# Revit family: 0040331 Sylvania Lighting Fixture Sylbay 4000K L4 37000LM AISLE PIR
name_source: partatom
category: Lighting Fixtures
revit_build: Autodesk Revit 2018 (Build: 20170223_1515(x64)
units: mm (PartAtom-declared; Revit-internal decimal feet)

## family parameters
Cut with Voids When Loaded = No
Host = Face
Light Source = No
OmniClass Number = 23.80.70.00
OmniClass Title = Lighting
Part Type = Normal
Room Calculation Point = No
Round Connector Dimension = Use Diameter
Shared = No

## types (1)
- 0040331 SYLBAY 4000K L4 37KLM AISLE PIR
    Apparent Load = 268 VA
    Assembly Code = D5020200
    AssetType = Fixed
    ClassificationName = Uniclass2015
    ClassificationValue = EF_70_80
    Cost = 0 $
    Default Elevation = 1219 mm
    Description = Logistics and Industry modular high bay luminaire with aisle optics to provide necessary illumination for narrow areas. Twin body with 4 optical modules, 37300 lumens, 268W, 139lm/W, 4000K, CRI 80, aisle beam optic.  Fitted with a high bay PIR for 360° detection up to 40m range at 15m mounting height. 3 step MacAdam ellipse, grey finish (RAL7012), Class 1, 220-240V, IP65, IK08 (sensor IK03), (LxWxH) 726x386x133mm, Mains + control cable of 2 meter.
    DocumentationLiterature = http://www.sylvania-lighting.com
    DurationUnit = hours
    ElectricShockClassification = 139
    ExpectedLife = 50000
    Height = 133 mm
    IfcExportAs = Class I
    IfcExportType = IfcLightFixtureType
    ImpactProtectionIndex = IfcLightFixtureType
    IngressProtection = IfcLightFixtureType
    InputNominalFrequency = 4000
    InputVoltage = 0
    LampColourRenderingIndex = 16500
    LampColourTemperature = LED
    LampMacAdamStep = 80
    LampNominalLuminous = 4000 K
    Length = 865 mm  [stored 2.83793 ft]
    LightOutputRatio = LED
    LuminaireType = 0
    ManufacturerName = 139 lm/W
    Material = Feilo Sylvania
    Material_1_FEILO = <By Category>
    Material_2_FEILO = <By Category>
    Material_3_FEILO = <By Category>
    Material_4_FEILO = <By Category>
    Model = Sylbay 4000K L4 37000LM AISLE PIR
    ModelNumber = 0040331
    ModelReference = Sylbay 4000K L4 37000LM AISLE PIR
    Name = Sylbay 4000K L4 37000LM AISLE PIR
    NominalDepth = 0 mm  [stored 0 ft]
    NominalHeight = 0 mm  [stored 0 ft]
    NominalLength = 386 mm  [stored 1.2664 ft]
    PowerConsumption = Lighting
    PowerFactor = 0
    Type Image = <None>
    TypeName = Sylbay 4000K L4 37000LM AISLE PIR
    URL = 0.98
    Voltage = 0 V
    WarrantyDescription = http://www.sylvania-lighting.com
    Width = 386 mm  [stored 1.2664 ft]

note: [stored X ft] marks values corroborated as IEEE doubles in the binary element streams (Revit-internal decimal feet)

## geometry (parser evidence)
native form markers: Sweep x3
no freeform markers — native parametric forms only
